# Revit family: TV-297
name_source: partatom
category: Plumbing Fixtures
revit_build: Autodesk Revit 2014 (Build: 20130308_1515(x64)
units: mm (PartAtom-declared; Revit-internal decimal feet)

## types (1)
- TV-297
    Batteries = Duracell DL-223 Or Panasonic CR-P2 Lithium Battery
    CW Connection = Yes
    Certification = http://www.helvex.com.mx
    Chrome = Brass Chromed
    Connection = ½" - 14 NPSM
    Description = Alpha Electronic Current Faucet Lavatory
    Detection Range = 1.9" (50 mm) - 8.7" (220 mm)
    Documentation = http://www.helvex.com.mx
    Features = Infrared Sensor, Filter with Check Valve Maintenance
    Feeding Voltage = 6 V
    Instructive = http://www.helvex.com.mx
    Manufacturer = Helvex
    Max. Working Pressure = 85.3 psi
    Min. Working Pressure = 5.7 psi
    Model = TV-297
    Type Comments = Electronic Line
    URL = http://www.helvex.com.mx

## geometry (parser evidence)
native form markers: Sweep x3
no freeform markers — native parametric forms only
